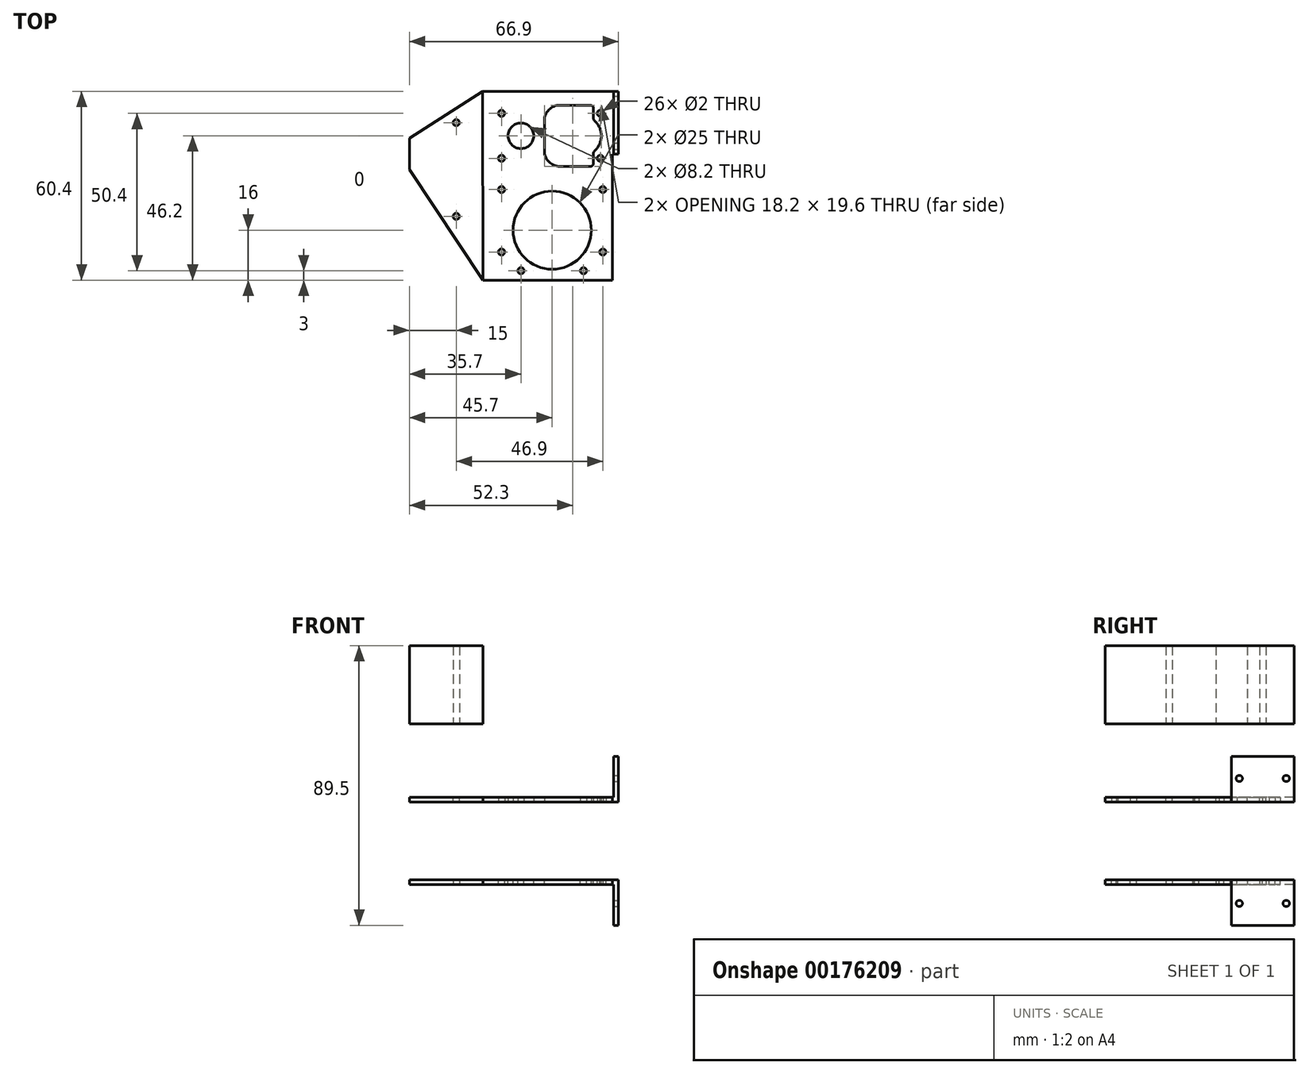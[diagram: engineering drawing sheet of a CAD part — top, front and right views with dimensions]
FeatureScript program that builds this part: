
annotation { "Feature Type Name" : "Feature", "Feature Type Description" : "" }
export const myFeature = defineFeature(function(context is Context, id is Id, definition is map)
    precondition{}
    {
        {
            var Q0;
            Q0=qCreatedBy(makeId("Top.planeOp"),FACE);
            var sketch = newSketch(context, id + "F0", { "sketchPlane" : qUnion([Q0])});
            skLineSegment(sketch, "E0.top", {"start": v(19.2, 14.2) * mm, "end": v(-19.2, 14.2) * mm});
            skLineSegment(sketch, "E0.left", {"start": v(19.2, -14.2) * mm, "end": v(19.2, 14.2) * mm});
            skLineSegment(sketch, "E0.right", {"start": v(-19.2, -14.2) * mm, "end": v(-19.2, 14.2) * mm});
            skPoint(sketch, "E0.middle", {"position": v(0, 0) * mm});
            skCircle(sketch, "E1", {"center": v(-10, 0) * mm, "radius": 4.1 * mm});
            skCircle(sketch, "E2", {"center": v(-16.2, 7.2) * mm, "radius": 1 * mm});
            skCircle(sketch, "E3", {"center": v(15.4, 7.2) * mm, "radius": 1 * mm});
            skLineSegment(sketch, "E4.bottom", {"start": v(2.5, 9.8) * mm, "end": v(12.2, 9.8) * mm});
            skLineSegment(sketch, "E4.top", {"start": v(2.5, -9.8) * mm, "end": v(12.2, -9.8) * mm});
            skLineSegment(sketch, "E4.left", {"start": v(-2.5, 4.8) * mm, "end": v(-2.5, -4.8) * mm});
            skLineSegment(sketch, "E4.right", {"start": v(13.2, 8.8) * mm, "end": v(13.2, 5.6) * mm});
            skPoint(sketch, "E4.middle", {"position": v(5.35, 0) * mm});
            skPoint(sketch, "E5.visualSharp", {"position": v(-2.5, 9.8) * mm});
            skArc(sketch, "E5.filletArc", {"start": v(2.5, 9.8) * mm, "mid": v(-1.04, 8.34) * mm, "end": v(-2.5, 4.8) * mm});
            skPoint(sketch, "E6.visualSharp", {"position": v(-2.5, -9.8) * mm});
            skArc(sketch, "E6.filletArc", {"start": v(-2.5, -4.8) * mm, "mid": v(-1.04, -8.34) * mm, "end": v(2.5, -9.8) * mm});
            skPoint(sketch, "E7.visualSharp", {"position": v(13.2, 9.8) * mm});
            skArc(sketch, "E7.filletArc", {"start": v(13.2, 8.8) * mm, "mid": v(12.9, 9.5) * mm, "end": v(12.2, 9.8) * mm});
            skPoint(sketch, "E8.visualSharp", {"position": v(13.2, -9.8) * mm});
            skArc(sketch, "E8.filletArc", {"start": v(12.2, -9.8) * mm, "mid": v(12.9, -9.5) * mm, "end": v(13.2, -8.8) * mm});
            skCircle(sketch, "E9.MirrorC", {"center": v(-16.2, -7.2) * mm, "radius": 1 * mm});
            skCircle(sketch, "E10.MirrorC", {"center": v(15.4, -7.2) * mm, "radius": 1 * mm});
            skArc(sketch, "E11", {"start": v(13.53, -4.84) * mm, "mid": v(15.7, 0) * mm, "end": v(13.53, 4.84) * mm});
            skLineSegment(sketch, "E12.trimOffspring", {"start": v(13.2, -5.6) * mm, "end": v(13.2, -8.8) * mm});
            skPoint(sketch, "E13.visualSharp", {"position": v(13.2, 5.12) * mm});
            skArc(sketch, "E13.filletArc", {"start": v(13.2, 5.6) * mm, "mid": v(13.29, 5.18) * mm, "end": v(13.53, 4.84) * mm});
            skPoint(sketch, "E14.visualSharp", {"position": v(13.2, -5.12) * mm});
            skArc(sketch, "E14.filletArc", {"start": v(13.53, -4.84) * mm, "mid": v(13.29, -5.18) * mm, "end": v(13.2, -5.6) * mm});
            skLineSegment(sketch, "E15.bottom", {"start": v(-19.2, -14.2) * mm, "end": v(19.2, -14.2) * mm, "construction": true});
            skLineSegment(sketch, "E15.top", {"start": v(-19.2, -46.2) * mm, "end": v(19.2, -46.2) * mm});
            skLineSegment(sketch, "E15.left", {"start": v(-19.2, -14.2) * mm, "end": v(-19.2, -46.2) * mm});
            skLineSegment(sketch, "E15.right", {"start": v(19.2, -14.2) * mm, "end": v(19.2, -46.2) * mm});
            skCircle(sketch, "E16", {"center": v(-10, -43.2) * mm, "radius": 1 * mm});
            skCircle(sketch, "E17.MirrorC", {"center": v(10, -43.2) * mm, "radius": 1 * mm});
            skCircle(sketch, "E18", {"center": v(16.2, -37.2) * mm, "radius": 1 * mm});
            skCircle(sketch, "E19", {"center": v(16.2, -17.2) * mm, "radius": 1 * mm});
            skCircle(sketch, "E20.MirrorC", {"center": v(-16.2, -17.2) * mm, "radius": 1 * mm});
            skCircle(sketch, "E21.MirrorC", {"center": v(-16.2, -37.2) * mm, "radius": 1 * mm});
            skCircle(sketch, "E22", {"center": v(0, -30.2) * mm, "radius": 12.5 * mm});
            skSolve(sketch);
        }
        {
            var Q0;
            Q0=qSketchRegion(id+"F0",true);
            extrude(context, id + "F1", {"entities" : qUnion([Q0]), "depth" : 1.5 * mm});
        }
        {
            var Q0;
            Q0=makeQuery(id+"F1.opExtrude","SWEPT_FACE",FACE,{"disambiguationData":[OSD([sQuery(id+"F0.wireOp",EDGE,"E0.left"),sQuery(id+"F0.wireOp",EDGE,"E15.right")])]});
            var sketch = newSketch(context, id + "F2", { "sketchPlane" : qUnion([Q0])});
            skLineSegment(sketch, "E23.bottom", {"start": v(14.2, 0) * mm, "end": v(-5.8, 0) * mm});
            skLineSegment(sketch, "E23.top", {"start": v(14.2, 1.5) * mm, "end": v(-5.8, 1.5) * mm});
            skLineSegment(sketch, "E23.left", {"start": v(14.2, 0) * mm, "end": v(14.2, 1.5) * mm});
            skLineSegment(sketch, "E23.right", {"start": v(-5.8, 0) * mm, "end": v(-5.8, 1.5) * mm});
            skSolve(sketch);
        }
        {
            var Q0;
            Q0=qSketchRegion(id+"F2",true);
            extrude(context, id + "F3", {"entities" : qUnion([Q0]), "operationType" : NewBodyOperationType.ADD, "depth" : 2 * mm});
        }
        {
            var Q0;
            Q0=makeQuery(id+"F3.boolean.opBoolean","MERGE",FACE,{"derivedFrom":[makeQuery(id+"F1.opExtrude","CAP_FACE",FACE,{"disambiguationData":[OSD([sQuery(id+"F0.wireOp",EDGE,"E0.top"),sQuery(id+"F0.wireOp",EDGE,"E0.left"),sQuery(id+"F0.wireOp",EDGE,"E0.right"),sQuery(id+"F0.wireOp",EDGE,"E1"),sQuery(id+"F0.wireOp",EDGE,"E2"),sQuery(id+"F0.wireOp",EDGE,"E3"),sQuery(id+"F0.wireOp",EDGE,"E4.bottom"),sQuery(id+"F0.wireOp",EDGE,"E4.top"),sQuery(id+"F0.wireOp",EDGE,"E4.left"),sQuery(id+"F0.wireOp",EDGE,"E4.right"),sQuery(id+"F0.wireOp",EDGE,"E5.filletArc"),sQuery(id+"F0.wireOp",EDGE,"E6.filletArc"),sQuery(id+"F0.wireOp",EDGE,"E7.filletArc"),sQuery(id+"F0.wireOp",EDGE,"E8.filletArc"),sQuery(id+"F0.wireOp",EDGE,"E9.MirrorC"),sQuery(id+"F0.wireOp",EDGE,"E10.MirrorC"),sQuery(id+"F0.wireOp",EDGE,"E11"),sQuery(id+"F0.wireOp",EDGE,"E12.trimOffspring"),sQuery(id+"F0.wireOp",EDGE,"E13.filletArc"),sQuery(id+"F0.wireOp",EDGE,"E14.filletArc"),sQuery(id+"F0.wireOp",EDGE,"E15.top"),sQuery(id+"F0.wireOp",EDGE,"E15.left"),sQuery(id+"F0.wireOp",EDGE,"E15.right"),sQuery(id+"F0.wireOp",EDGE,"E16"),sQuery(id+"F0.wireOp",EDGE,"E17.MirrorC"),sQuery(id+"F0.wireOp",EDGE,"E18"),sQuery(id+"F0.wireOp",EDGE,"E19"),sQuery(id+"F0.wireOp",EDGE,"E20.MirrorC"),sQuery(id+"F0.wireOp",EDGE,"E21.MirrorC")])],"isStart":false}),makeQuery(id+"F3.opExtrude","SWEPT_FACE",FACE,{"disambiguationData":[OSD([sQuery(id+"F2.wireOp",EDGE,"E23.top")])]})]});
            var sketch = newSketch(context, id + "F4", { "sketchPlane" : qUnion([Q0])});
            skLineSegment(sketch, "E24.bottom", {"start": v(19.7, 14.2) * mm, "end": v(21.2, 14.2) * mm});
            skLineSegment(sketch, "E24.top", {"start": v(19.7, -5.8) * mm, "end": v(21.2, -5.8) * mm});
            skLineSegment(sketch, "E24.left", {"start": v(19.7, 14.2) * mm, "end": v(19.7, -5.8) * mm});
            skLineSegment(sketch, "E24.right", {"start": v(21.2, 14.2) * mm, "end": v(21.2, -5.8) * mm});
            skSolve(sketch);
        }
        {
            var Q0;
            Q0=qSketchRegion(id+"F4",true);
            extrude(context, id + "F5", {"entities" : qUnion([Q0]), "operationType" : NewBodyOperationType.ADD, "depth" : 13 * mm});
        }
        {
            var Q0;
            Q0=qCreatedBy(makeId("Top.planeOp"),FACE);
            cPlane(context, id + "F6", {"entities" : qUnion([Q0]), "cplaneType" : CPlaneType.OFFSET, "offset" : (25 / 2) * mm, "oppositeDirection" : true, "width" : 150 * mm, "height" : 150 * mm});
        }
        {
            var Q0;
            Q0=makeQuery(id+"F1.opExtrude","SWEPT_BODY",BODY,{"disambiguationData":[OSD([sQuery(id+"F0.wireOp",EDGE,"E0.top"),sQuery(id+"F0.wireOp",EDGE,"E0.left"),sQuery(id+"F0.wireOp",EDGE,"E0.right"),sQuery(id+"F0.wireOp",EDGE,"E1"),sQuery(id+"F0.wireOp",EDGE,"E2"),sQuery(id+"F0.wireOp",EDGE,"E3"),sQuery(id+"F0.wireOp",EDGE,"E4.bottom"),sQuery(id+"F0.wireOp",EDGE,"E4.top"),sQuery(id+"F0.wireOp",EDGE,"E4.left"),sQuery(id+"F0.wireOp",EDGE,"E4.right"),sQuery(id+"F0.wireOp",EDGE,"E5.filletArc"),sQuery(id+"F0.wireOp",EDGE,"E6.filletArc"),sQuery(id+"F0.wireOp",EDGE,"E7.filletArc"),sQuery(id+"F0.wireOp",EDGE,"E8.filletArc"),sQuery(id+"F0.wireOp",EDGE,"E9.MirrorC"),sQuery(id+"F0.wireOp",EDGE,"E10.MirrorC"),sQuery(id+"F0.wireOp",EDGE,"E11"),sQuery(id+"F0.wireOp",EDGE,"E12.trimOffspring"),sQuery(id+"F0.wireOp",EDGE,"E13.filletArc"),sQuery(id+"F0.wireOp",EDGE,"E14.filletArc"),sQuery(id+"F0.wireOp",EDGE,"E15.top"),sQuery(id+"F0.wireOp",EDGE,"E15.left"),sQuery(id+"F0.wireOp",EDGE,"E15.right"),sQuery(id+"F0.wireOp",EDGE,"E16"),sQuery(id+"F0.wireOp",EDGE,"E17.MirrorC"),sQuery(id+"F0.wireOp",EDGE,"E18"),sQuery(id+"F0.wireOp",EDGE,"E19"),sQuery(id+"F0.wireOp",EDGE,"E20.MirrorC"),sQuery(id+"F0.wireOp",EDGE,"E21.MirrorC")])]});
            var Q1;
            Q1=qCreatedBy(id+"F6.planeOp",FACE);
            mirror(context, id + "F7", {"entities" : qUnion([Q0]), "mirrorPlane" : qUnion([Q1])});
        }
        {
            var Q0;
            Q0=makeQuery(id+"F7.opPattern","COPY",FACE,{"derivedFrom":makeQuery(id+"F5.boolean.opBoolean","MERGE",FACE,{"derivedFrom":[makeQuery(id+"F3.opExtrude","CAP_FACE",FACE,{"disambiguationData":[OSD([sQuery(id+"F2.wireOp",EDGE,"E23.bottom"),sQuery(id+"F2.wireOp",EDGE,"E23.top"),sQuery(id+"F2.wireOp",EDGE,"E23.left"),sQuery(id+"F2.wireOp",EDGE,"E23.right")])],"isStart":false}),makeQuery(id+"F5.opExtrude","SWEPT_FACE",FACE,{"disambiguationData":[OSD([sQuery(id+"F4.wireOp",EDGE,"E24.right")])]})]}),"instanceName":"1"});
            var sketch = newSketch(context, id + "F8", { "sketchPlane" : qUnion([Q0])});
            skCircle(sketch, "E25", {"center": v(11.7, 7.5) * mm, "radius": 1 * mm});
            skCircle(sketch, "E26", {"center": v(-3.3, 7.5) * mm, "radius": 1 * mm});
            skCircle(sketch, "E27.MirrorC", {"center": v(11.7, -32.5) * mm, "radius": 1 * mm});
            skCircle(sketch, "E28.MirrorC", {"center": v(-3.3, -32.5) * mm, "radius": 1 * mm});
            skSolve(sketch);
        }
        {
            var Q0;
            Q0=qSketchRegion(id+"F8",true);
            extrude(context, id + "F9", {"entities" : qUnion([Q0]), "operationType" : NewBodyOperationType.REMOVE, "endBound" : BoundingType.UP_TO_NEXT, "oppositeDirection" : true, "depth" : 25 * mm});
        }
        {
            var Q0;
            Q0=makeQuery(id+"F1.opExtrude","SWEPT_FACE",FACE,{"disambiguationData":[OSD([sQuery(id+"F0.wireOp",EDGE,"E0.right"),sQuery(id+"F0.wireOp",EDGE,"E15.left")])]});
            var sketch = newSketch(context, id + "F10", { "sketchPlane" : qUnion([Q0])});
            skLineSegment(sketch, "E29.bottom", {"start": v(-14.2, 0) * mm, "end": v(46.2, 0) * mm});
            skLineSegment(sketch, "E29.top", {"start": v(-14.2, 1.5) * mm, "end": v(46.2, 1.5) * mm});
            skLineSegment(sketch, "E29.left", {"start": v(-14.2, 0) * mm, "end": v(-14.2, 1.5) * mm});
            skLineSegment(sketch, "E29.right", {"start": v(46.2, 0) * mm, "end": v(46.2, 1.5) * mm});
            skSolve(sketch);
        }
        {
            var Q0;
            Q0=qSketchRegion(id+"F10",true);
            extrude(context, id + "F11", {"entities" : qUnion([Q0]), "operationType" : NewBodyOperationType.ADD, "depth" : (25 + 1.5) * mm});
        }
        {
            var Q0;
            Q0=makeQuery(id+"F11.boolean.opBoolean","MERGE",FACE,{"derivedFrom":[makeQuery(id+"F3.boolean.opBoolean","MERGE",FACE,{"derivedFrom":[makeQuery(id+"F1.opExtrude","CAP_FACE",FACE,{"disambiguationData":[OSD([sQuery(id+"F0.wireOp",EDGE,"E0.top"),sQuery(id+"F0.wireOp",EDGE,"E0.left"),sQuery(id+"F0.wireOp",EDGE,"E0.right"),sQuery(id+"F0.wireOp",EDGE,"E1"),sQuery(id+"F0.wireOp",EDGE,"E2"),sQuery(id+"F0.wireOp",EDGE,"E3"),sQuery(id+"F0.wireOp",EDGE,"E4.bottom"),sQuery(id+"F0.wireOp",EDGE,"E4.top"),sQuery(id+"F0.wireOp",EDGE,"E4.left"),sQuery(id+"F0.wireOp",EDGE,"E4.right"),sQuery(id+"F0.wireOp",EDGE,"E5.filletArc"),sQuery(id+"F0.wireOp",EDGE,"E6.filletArc"),sQuery(id+"F0.wireOp",EDGE,"E7.filletArc"),sQuery(id+"F0.wireOp",EDGE,"E8.filletArc"),sQuery(id+"F0.wireOp",EDGE,"E9.MirrorC"),sQuery(id+"F0.wireOp",EDGE,"E10.MirrorC"),sQuery(id+"F0.wireOp",EDGE,"E11"),sQuery(id+"F0.wireOp",EDGE,"E12.trimOffspring"),sQuery(id+"F0.wireOp",EDGE,"E13.filletArc"),sQuery(id+"F0.wireOp",EDGE,"E14.filletArc"),sQuery(id+"F0.wireOp",EDGE,"E15.top"),sQuery(id+"F0.wireOp",EDGE,"E15.left"),sQuery(id+"F0.wireOp",EDGE,"E15.right"),sQuery(id+"F0.wireOp",EDGE,"E16"),sQuery(id+"F0.wireOp",EDGE,"E17.MirrorC"),sQuery(id+"F0.wireOp",EDGE,"E18"),sQuery(id+"F0.wireOp",EDGE,"E19"),sQuery(id+"F0.wireOp",EDGE,"E20.MirrorC"),sQuery(id+"F0.wireOp",EDGE,"E21.MirrorC")])],"isStart":false}),makeQuery(id+"F3.opExtrude","SWEPT_FACE",FACE,{"disambiguationData":[OSD([sQuery(id+"F2.wireOp",EDGE,"E23.top")])]})]}),makeQuery(id+"F11.opExtrude","SWEPT_FACE",FACE,{"disambiguationData":[OSD([sQuery(id+"F10.wireOp",EDGE,"E29.top")])]})]});
            var sketch = newSketch(context, id + "F12", { "sketchPlane" : qUnion([Q0])});
            skLineSegment(sketch, "E30", {"start": v(-20.7, 14.2) * mm, "end": v(-20.7, -46.2) * mm, "construction": true});
            skLineSegment(sketch, "E31", {"start": v(-22.25, 14.2) * mm, "end": v(-45.7, -0.8) * mm});
            skLineSegment(sketch, "E32", {"start": v(-45.7, -0.8) * mm, "end": v(-45.7, -10.8) * mm});
            skLineSegment(sketch, "E33", {"start": v(-45.7, -10.8) * mm, "end": v(-22.2, -46.2) * mm});
            skLineSegment(sketch, "E34", {"start": v(-22.2, -46.2) * mm, "end": v(-45.7, -46.2) * mm});
            skLineSegment(sketch, "E35", {"start": v(-45.7, -46.2) * mm, "end": v(-45.7, -10.8) * mm});
            skLineSegment(sketch, "E36", {"start": v(-22.25, 14.2) * mm, "end": v(-45.7, 14.2) * mm});
            skLineSegment(sketch, "E37", {"start": v(-45.7, 14.2) * mm, "end": v(-45.7, -0.8) * mm});
            skCircle(sketch, "E38", {"center": v(-30.7, 4.2) * mm, "radius": 1 * mm});
            skCircle(sketch, "E39", {"center": v(-30.7, -25.8) * mm, "radius": 1 * mm});
            skLineSegment(sketch, "E40", {"start": v(-30.7, 4.2) * mm, "end": v(-30.7, -25.8) * mm, "construction": true});
            skSolve(sketch);
        }
        {
            var Q0;
            Q0=qSketchRegion(id+"F12",true);
            extrude(context, id + "F13", {"entities" : qUnion([Q0]), "operationType" : NewBodyOperationType.REMOVE, "endBound" : BoundingType.UP_TO_NEXT, "oppositeDirection" : true, "depth" : 25 * mm});
        }
        {
            var Q0;
            Q0=makeQuery(id+"F1.opExtrude","SWEPT_BODY",BODY,{"disambiguationData":[OSD([sQuery(id+"F0.wireOp",EDGE,"E0.top"),sQuery(id+"F0.wireOp",EDGE,"E0.left"),sQuery(id+"F0.wireOp",EDGE,"E0.right"),sQuery(id+"F0.wireOp",EDGE,"E1"),sQuery(id+"F0.wireOp",EDGE,"E2"),sQuery(id+"F0.wireOp",EDGE,"E3"),sQuery(id+"F0.wireOp",EDGE,"E4.bottom"),sQuery(id+"F0.wireOp",EDGE,"E4.top"),sQuery(id+"F0.wireOp",EDGE,"E4.left"),sQuery(id+"F0.wireOp",EDGE,"E4.right"),sQuery(id+"F0.wireOp",EDGE,"E5.filletArc"),sQuery(id+"F0.wireOp",EDGE,"E6.filletArc"),sQuery(id+"F0.wireOp",EDGE,"E7.filletArc"),sQuery(id+"F0.wireOp",EDGE,"E8.filletArc"),sQuery(id+"F0.wireOp",EDGE,"E9.MirrorC"),sQuery(id+"F0.wireOp",EDGE,"E10.MirrorC"),sQuery(id+"F0.wireOp",EDGE,"E11"),sQuery(id+"F0.wireOp",EDGE,"E12.trimOffspring"),sQuery(id+"F0.wireOp",EDGE,"E13.filletArc"),sQuery(id+"F0.wireOp",EDGE,"E14.filletArc"),sQuery(id+"F0.wireOp",EDGE,"E15.top"),sQuery(id+"F0.wireOp",EDGE,"E15.left"),sQuery(id+"F0.wireOp",EDGE,"E15.right"),sQuery(id+"F0.wireOp",EDGE,"E16"),sQuery(id+"F0.wireOp",EDGE,"E17.MirrorC"),sQuery(id+"F0.wireOp",EDGE,"E18"),sQuery(id+"F0.wireOp",EDGE,"E19"),sQuery(id+"F0.wireOp",EDGE,"E20.MirrorC"),sQuery(id+"F0.wireOp",EDGE,"E21.MirrorC")])]});
            var Q1;
            Q1=qCreatedBy(id+"F6.planeOp",FACE);
            mirror(context, id + "F14", {"operationType" : NewBodyOperationType.ADD, "entities" : qUnion([Q0]), "mirrorPlane" : qUnion([Q1])});
        }
        {
            var Q0;
            Q0=qCreatedBy(makeId("Top.planeOp"),FACE);
            cPlane(context, id + "F15", {"entities" : qUnion([Q0]), "cplaneType" : CPlaneType.OFFSET, "offset" : 25 * mm, "width" : 150 * mm, "height" : 150 * mm});
        }
        {
            var Q0;
            Q0=qCreatedBy(id+"F15.planeOp",FACE);
            var sketch = newSketch(context, id + "F16", { "sketchPlane" : qUnion([Q0])});
            skLineSegment(sketch, "E41.0.0", {"start": v(19.7, 14.2) * mm, "end": v(-22.25, 14.2) * mm, "construction": true});
            skLineSegment(sketch, "E41.0.1", {"start": v(-22.25, 14.2) * mm, "end": v(-45.7, -0.8) * mm});
            skLineSegment(sketch, "E41.0.2", {"start": v(-45.7, -0.8) * mm, "end": v(-45.7, -10.8) * mm});
            skLineSegment(sketch, "E41.0.3", {"start": v(-45.7, -10.8) * mm, "end": v(-22.2, -46.2) * mm});
            skLineSegment(sketch, "E41.0.4", {"start": v(-22.2, -46.2) * mm, "end": v(19.2, -46.2) * mm, "construction": true});
            skLineSegment(sketch, "E41.0.5", {"start": v(19.2, -46.2) * mm, "end": v(19.2, -5.8) * mm, "construction": true});
            skLineSegment(sketch, "E41.0.6", {"start": v(19.2, -5.8) * mm, "end": v(19.7, -5.8) * mm, "construction": true});
            skLineSegment(sketch, "E41.0.7", {"start": v(19.7, -5.8) * mm, "end": v(19.7, 14.2) * mm, "construction": true});
            skLineSegment(sketch, "E42", {"start": v(-22.25, 14.2) * mm, "end": v(-22.2, -46.2) * mm});
            skCircle(sketch, "E43.0", {"center": v(-30.7, 4.2) * mm, "radius": 1 * mm});
            skCircle(sketch, "E43.1", {"center": v(-30.7, -25.8) * mm, "radius": 1 * mm});
            skCircle(sketch, "E43.2", {"center": v(-30.7, 4.2) * mm, "radius": 1 * mm});
            skCircle(sketch, "E43.3", {"center": v(-30.7, -25.8) * mm, "radius": 1 * mm});
            skCircle(sketch, "E43.4", {"center": v(-30.7, 4.2) * mm, "radius": 1 * mm});
            skCircle(sketch, "E43.5", {"center": v(-30.7, -25.8) * mm, "radius": 1 * mm});
            skCircle(sketch, "E43.6", {"center": v(-30.7, -25.8) * mm, "radius": 1 * mm});
            skCircle(sketch, "E43.7", {"center": v(-30.7, 4.2) * mm, "radius": 1 * mm});
            skSolve(sketch);
        }
        {
            var Q0;
            Q0=qSketchRegion(id+"F16",true);
            extrude(context, id + "F17", {"entities" : qUnion([Q0]), "depth" : 25 * mm});
        }
    });
